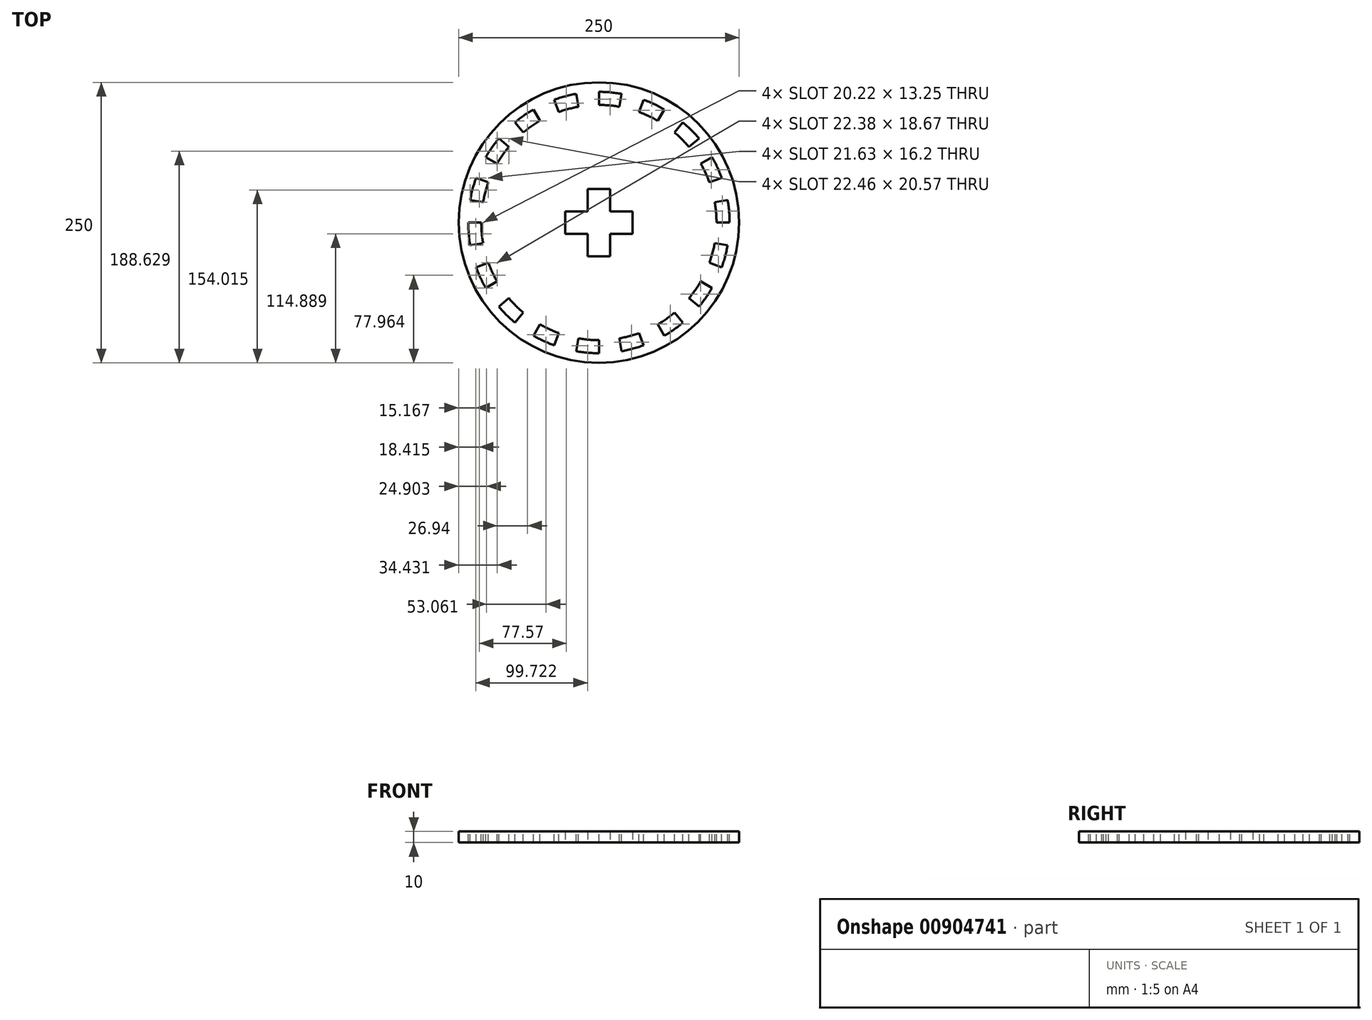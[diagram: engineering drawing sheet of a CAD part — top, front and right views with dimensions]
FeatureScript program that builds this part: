
annotation { "Feature Type Name" : "Feature", "Feature Type Description" : "" }
export const myFeature = defineFeature(function(context is Context, id is Id, definition is map)
    precondition{}
    {
        {
            var Q0;
            Q0=qCreatedBy(makeId("Top.planeOp"),FACE);
            var sketch = newSketch(context, id + "F0", { "sketchPlane" : qUnion([Q0])});
            skCircle(sketch, "E0", {"center": v(0, 0) * mm, "radius": 145 * mm});
            skArc(sketch, "E1", {"start": v(9.54, 136.41) * mm, "mid": v(4.77, 136.66) * mm, "end": v(0, 136.75) * mm});
            skArc(sketch, "E2", {"start": v(8, 114.55) * mm, "mid": v(4, 114.76) * mm, "end": v(0, 114.83) * mm});
            skLineSegment(sketch, "E3", {"start": v(0, 0) * mm, "end": v(0, 38.61) * mm, "construction": true});
            skLineSegment(sketch, "E4", {"start": v(0, 38.61) * mm, "end": v(0, 0) * mm, "construction": true});
            skLineSegment(sketch, "E5", {"start": v(0, 0) * mm, "end": v(-47.77, 0) * mm, "construction": true});
            skLineSegment(sketch, "E6", {"start": v(0, 30) * mm, "end": v(-10, 30) * mm});
            skLineSegment(sketch, "E7", {"start": v(-10, 30) * mm, "end": v(-10, 10) * mm});
            skLineSegment(sketch, "E8", {"start": v(-10, 10) * mm, "end": v(-30, 10) * mm});
            skLineSegment(sketch, "E9", {"start": v(-30, 10) * mm, "end": v(-30, 0) * mm});
            skLineSegment(sketch, "E10.MirrorCS", {"start": v(-30, -10) * mm, "end": v(-30, 0) * mm});
            skLineSegment(sketch, "E11.MirrorCS", {"start": v(-10, -10) * mm, "end": v(-30, -10) * mm});
            skLineSegment(sketch, "E12.MirrorCS", {"start": v(-10, -30) * mm, "end": v(-10, -10) * mm});
            skLineSegment(sketch, "E13.MirrorCS", {"start": v(0, -30) * mm, "end": v(-10, -30) * mm});
            skLineSegment(sketch, "E14.MirrorCS", {"start": v(0, 30) * mm, "end": v(10, 30) * mm});
            skLineSegment(sketch, "E15.MirrorCS", {"start": v(10, 30) * mm, "end": v(10, 10) * mm});
            skLineSegment(sketch, "E16.MirrorCS", {"start": v(10, 10) * mm, "end": v(30, 10) * mm});
            skLineSegment(sketch, "E17.MirrorCS", {"start": v(30, 10) * mm, "end": v(30, 0) * mm});
            skLineSegment(sketch, "E18.MirrorCS", {"start": v(30, -10) * mm, "end": v(30, 0) * mm});
            skLineSegment(sketch, "E19.MirrorCS", {"start": v(10, -10) * mm, "end": v(30, -10) * mm});
            skLineSegment(sketch, "E20.MirrorCS", {"start": v(0, -30) * mm, "end": v(10, -30) * mm});
            skLineSegment(sketch, "E21.MirrorCS", {"start": v(10, -30) * mm, "end": v(10, -10) * mm});
            skLineSegment(sketch, "E22", {"start": v(0, 114.83) * mm, "end": v(0, 136.75) * mm});
            skLineSegment(sketch, "E23", {"start": v(8, 114.55) * mm, "end": v(9.54, 136.41) * mm});
            skArc(sketch, "E24.1.0", {"start": v(-10, 114.4) * mm, "mid": v(-14, 113.98) * mm, "end": v(-17.96, 113.42) * mm});
            skLineSegment(sketch, "E24.1.1", {"start": v(-17.96, 113.42) * mm, "end": v(-21.4, 135.06) * mm});
            skArc(sketch, "E24.1.2", {"start": v(-11.92, 136.23) * mm, "mid": v(-16.67, 135.73) * mm, "end": v(-21.4, 135.06) * mm});
            skLineSegment(sketch, "E24.1.3", {"start": v(-10, 114.4) * mm, "end": v(-11.92, 136.23) * mm});
            skArc(sketch, "E24.2.0", {"start": v(-27.78, 111.42) * mm, "mid": v(-31.65, 110.39) * mm, "end": v(-35.49, 109.21) * mm});
            skLineSegment(sketch, "E24.2.1", {"start": v(-35.49, 109.21) * mm, "end": v(-42.26, 130.05) * mm});
            skArc(sketch, "E24.2.2", {"start": v(-33.08, 132.68) * mm, "mid": v(-37.7, 131.45) * mm, "end": v(-42.26, 130.05) * mm});
            skLineSegment(sketch, "E24.2.3", {"start": v(-27.78, 111.42) * mm, "end": v(-33.08, 132.68) * mm});
            skArc(sketch, "E24.3.0", {"start": v(-44.87, 105.7) * mm, "mid": v(-48.53, 104.07) * mm, "end": v(-52.13, 102.32) * mm});
            skLineSegment(sketch, "E24.3.1", {"start": v(-52.13, 102.32) * mm, "end": v(-62.08, 121.84) * mm});
            skArc(sketch, "E24.3.2", {"start": v(-53.43, 125.88) * mm, "mid": v(-57.8, 123.93) * mm, "end": v(-62.08, 121.84) * mm});
            skLineSegment(sketch, "E24.3.3", {"start": v(-44.87, 105.7) * mm, "end": v(-53.43, 125.88) * mm});
            skArc(sketch, "E24.4.0", {"start": v(-60.85, 97.38) * mm, "mid": v(-64.21, 95.2) * mm, "end": v(-67.5, 92.9) * mm});
            skLineSegment(sketch, "E24.4.1", {"start": v(-67.5, 92.9) * mm, "end": v(-80.38, 110.63) * mm});
            skArc(sketch, "E24.4.2", {"start": v(-72.47, 115.97) * mm, "mid": v(-76.47, 113.37) * mm, "end": v(-80.38, 110.63) * mm});
            skLineSegment(sketch, "E24.4.3", {"start": v(-60.85, 97.38) * mm, "end": v(-72.47, 115.97) * mm});
            skArc(sketch, "E24.5.0", {"start": v(-75.34, 86.67) * mm, "mid": v(-78.32, 83.98) * mm, "end": v(-81.2, 81.2) * mm});
            skLineSegment(sketch, "E24.5.1", {"start": v(-81.2, 81.2) * mm, "end": v(-96.7, 96.7) * mm});
            skArc(sketch, "E24.5.2", {"start": v(-89.71, 103.2) * mm, "mid": v(-93.26, 100.01) * mm, "end": v(-96.7, 96.7) * mm});
            skLineSegment(sketch, "E24.5.3", {"start": v(-75.34, 86.67) * mm, "end": v(-89.71, 103.2) * mm});
            skArc(sketch, "E24.6.0", {"start": v(-87.97, 73.81) * mm, "mid": v(-90.5, 70.7) * mm, "end": v(-92.9, 67.5) * mm});
            skLineSegment(sketch, "E24.6.1", {"start": v(-92.9, 67.5) * mm, "end": v(-110.63, 80.38) * mm});
            skArc(sketch, "E24.6.2", {"start": v(-104.75, 87.9) * mm, "mid": v(-107.76, 84.19) * mm, "end": v(-110.63, 80.38) * mm});
            skLineSegment(sketch, "E24.6.3", {"start": v(-87.97, 73.81) * mm, "end": v(-104.75, 87.9) * mm});
            skArc(sketch, "E24.7.0", {"start": v(-98.43, 59.14) * mm, "mid": v(-100.44, 55.67) * mm, "end": v(-102.32, 52.13) * mm});
            skLineSegment(sketch, "E24.7.1", {"start": v(-102.32, 52.13) * mm, "end": v(-121.84, 62.08) * mm});
            skArc(sketch, "E24.7.2", {"start": v(-117.22, 70.43) * mm, "mid": v(-119.6, 66.3) * mm, "end": v(-121.84, 62.08) * mm});
            skLineSegment(sketch, "E24.7.3", {"start": v(-98.43, 59.14) * mm, "end": v(-117.22, 70.43) * mm});
            skArc(sketch, "E24.8.0", {"start": v(-106.47, 43.02) * mm, "mid": v(-107.9, 39.28) * mm, "end": v(-109.21, 35.49) * mm});
            skLineSegment(sketch, "E24.8.1", {"start": v(-109.21, 35.49) * mm, "end": v(-130.05, 42.26) * mm});
            skArc(sketch, "E24.8.2", {"start": v(-126.79, 51.23) * mm, "mid": v(-128.5, 46.77) * mm, "end": v(-130.05, 42.26) * mm});
            skLineSegment(sketch, "E24.8.3", {"start": v(-106.47, 43.02) * mm, "end": v(-126.79, 51.23) * mm});
            skArc(sketch, "E24.9.0", {"start": v(-111.9, 25.83) * mm, "mid": v(-112.72, 21.91) * mm, "end": v(-113.42, 17.96) * mm});
            skLineSegment(sketch, "E24.9.1", {"start": v(-113.42, 17.96) * mm, "end": v(-135.06, 21.4) * mm});
            skArc(sketch, "E24.9.2", {"start": v(-133.24, 30.76) * mm, "mid": v(-134.23, 26.1) * mm, "end": v(-135.06, 21.4) * mm});
            skLineSegment(sketch, "E24.9.3", {"start": v(-111.9, 25.83) * mm, "end": v(-133.24, 30.76) * mm});
            skArc(sketch, "E24.10.0", {"start": v(-114.55, 8) * mm, "mid": v(-114.76, 4) * mm, "end": v(-114.83, 0) * mm});
            skLineSegment(sketch, "E24.10.1", {"start": v(-114.83, 0) * mm, "end": v(-136.75, 0) * mm});
            skArc(sketch, "E24.10.2", {"start": v(-136.41, 9.54) * mm, "mid": v(-136.66, 4.77) * mm, "end": v(-136.75, 0) * mm});
            skLineSegment(sketch, "E24.10.3", {"start": v(-114.55, 8) * mm, "end": v(-136.41, 9.54) * mm});
            skArc(sketch, "E24.11.0", {"start": v(-114.4, -10) * mm, "mid": v(-113.98, -14) * mm, "end": v(-113.42, -17.96) * mm});
            skLineSegment(sketch, "E24.11.1", {"start": v(-113.42, -17.96) * mm, "end": v(-135.06, -21.4) * mm});
            skArc(sketch, "E24.11.2", {"start": v(-136.23, -11.92) * mm, "mid": v(-135.73, -16.67) * mm, "end": v(-135.06, -21.4) * mm});
            skLineSegment(sketch, "E24.11.3", {"start": v(-114.4, -10) * mm, "end": v(-136.23, -11.92) * mm});
            skArc(sketch, "E24.12.0", {"start": v(-111.42, -27.78) * mm, "mid": v(-110.39, -31.65) * mm, "end": v(-109.21, -35.49) * mm});
            skLineSegment(sketch, "E24.12.1", {"start": v(-109.21, -35.49) * mm, "end": v(-130.05, -42.26) * mm});
            skArc(sketch, "E24.12.2", {"start": v(-132.68, -33.08) * mm, "mid": v(-131.45, -37.7) * mm, "end": v(-130.05, -42.26) * mm});
            skLineSegment(sketch, "E24.12.3", {"start": v(-111.42, -27.78) * mm, "end": v(-132.68, -33.08) * mm});
            skArc(sketch, "E24.13.0", {"start": v(-105.7, -44.87) * mm, "mid": v(-104.07, -48.53) * mm, "end": v(-102.32, -52.13) * mm});
            skLineSegment(sketch, "E24.13.1", {"start": v(-102.32, -52.13) * mm, "end": v(-121.84, -62.08) * mm});
            skArc(sketch, "E24.13.2", {"start": v(-125.88, -53.43) * mm, "mid": v(-123.93, -57.8) * mm, "end": v(-121.84, -62.08) * mm});
            skLineSegment(sketch, "E24.13.3", {"start": v(-105.7, -44.87) * mm, "end": v(-125.88, -53.43) * mm});
            skArc(sketch, "E24.14.0", {"start": v(-97.38, -60.85) * mm, "mid": v(-95.2, -64.21) * mm, "end": v(-92.9, -67.5) * mm});
            skLineSegment(sketch, "E24.14.1", {"start": v(-92.9, -67.5) * mm, "end": v(-110.63, -80.38) * mm});
            skArc(sketch, "E24.14.2", {"start": v(-115.97, -72.47) * mm, "mid": v(-113.37, -76.47) * mm, "end": v(-110.63, -80.38) * mm});
            skLineSegment(sketch, "E24.14.3", {"start": v(-97.38, -60.85) * mm, "end": v(-115.97, -72.47) * mm});
            skArc(sketch, "E24.15.0", {"start": v(-86.67, -75.34) * mm, "mid": v(-83.98, -78.32) * mm, "end": v(-81.2, -81.2) * mm});
            skLineSegment(sketch, "E24.15.1", {"start": v(-81.2, -81.2) * mm, "end": v(-96.7, -96.7) * mm});
            skArc(sketch, "E24.15.2", {"start": v(-103.2, -89.71) * mm, "mid": v(-100.01, -93.26) * mm, "end": v(-96.7, -96.7) * mm});
            skLineSegment(sketch, "E24.15.3", {"start": v(-86.67, -75.34) * mm, "end": v(-103.2, -89.71) * mm});
            skArc(sketch, "E24.16.0", {"start": v(-73.81, -87.97) * mm, "mid": v(-70.7, -90.5) * mm, "end": v(-67.5, -92.9) * mm});
            skLineSegment(sketch, "E24.16.1", {"start": v(-67.5, -92.9) * mm, "end": v(-80.38, -110.63) * mm});
            skArc(sketch, "E24.16.2", {"start": v(-87.9, -104.75) * mm, "mid": v(-84.19, -107.76) * mm, "end": v(-80.38, -110.63) * mm});
            skLineSegment(sketch, "E24.16.3", {"start": v(-73.81, -87.97) * mm, "end": v(-87.9, -104.75) * mm});
            skArc(sketch, "E24.17.0", {"start": v(-59.14, -98.43) * mm, "mid": v(-55.67, -100.44) * mm, "end": v(-52.13, -102.32) * mm});
            skLineSegment(sketch, "E24.17.1", {"start": v(-52.13, -102.32) * mm, "end": v(-62.08, -121.84) * mm});
            skArc(sketch, "E24.17.2", {"start": v(-70.43, -117.22) * mm, "mid": v(-66.3, -119.6) * mm, "end": v(-62.08, -121.84) * mm});
            skLineSegment(sketch, "E24.17.3", {"start": v(-59.14, -98.43) * mm, "end": v(-70.43, -117.22) * mm});
            skArc(sketch, "E24.18.0", {"start": v(-43.02, -106.47) * mm, "mid": v(-39.28, -107.9) * mm, "end": v(-35.49, -109.21) * mm});
            skLineSegment(sketch, "E24.18.1", {"start": v(-35.49, -109.21) * mm, "end": v(-42.26, -130.05) * mm});
            skArc(sketch, "E24.18.2", {"start": v(-51.23, -126.79) * mm, "mid": v(-46.77, -128.5) * mm, "end": v(-42.26, -130.05) * mm});
            skLineSegment(sketch, "E24.18.3", {"start": v(-43.02, -106.47) * mm, "end": v(-51.23, -126.79) * mm});
            skArc(sketch, "E24.19.0", {"start": v(-25.83, -111.9) * mm, "mid": v(-21.91, -112.72) * mm, "end": v(-17.96, -113.42) * mm});
            skLineSegment(sketch, "E24.19.1", {"start": v(-17.96, -113.42) * mm, "end": v(-21.4, -135.06) * mm});
            skArc(sketch, "E24.19.2", {"start": v(-30.76, -133.24) * mm, "mid": v(-26.1, -134.23) * mm, "end": v(-21.4, -135.06) * mm});
            skLineSegment(sketch, "E24.19.3", {"start": v(-25.83, -111.9) * mm, "end": v(-30.76, -133.24) * mm});
            skArc(sketch, "E24.20.0", {"start": v(-8, -114.55) * mm, "mid": v(-4, -114.76) * mm, "end": v(0, -114.83) * mm});
            skLineSegment(sketch, "E24.20.1", {"start": v(0, -114.83) * mm, "end": v(0, -136.75) * mm});
            skArc(sketch, "E24.20.2", {"start": v(-9.54, -136.41) * mm, "mid": v(-4.77, -136.66) * mm, "end": v(0, -136.75) * mm});
            skLineSegment(sketch, "E24.20.3", {"start": v(-8, -114.55) * mm, "end": v(-9.54, -136.41) * mm});
            skArc(sketch, "E24.21.0", {"start": v(10, -114.4) * mm, "mid": v(14, -113.98) * mm, "end": v(17.96, -113.42) * mm});
            skLineSegment(sketch, "E24.21.1", {"start": v(17.96, -113.42) * mm, "end": v(21.4, -135.06) * mm});
            skArc(sketch, "E24.21.2", {"start": v(11.92, -136.23) * mm, "mid": v(16.67, -135.73) * mm, "end": v(21.4, -135.06) * mm});
            skLineSegment(sketch, "E24.21.3", {"start": v(10, -114.4) * mm, "end": v(11.92, -136.23) * mm});
            skArc(sketch, "E24.22.0", {"start": v(27.78, -111.42) * mm, "mid": v(31.65, -110.39) * mm, "end": v(35.49, -109.21) * mm});
            skLineSegment(sketch, "E24.22.1", {"start": v(35.49, -109.21) * mm, "end": v(42.26, -130.05) * mm});
            skArc(sketch, "E24.22.2", {"start": v(33.08, -132.68) * mm, "mid": v(37.7, -131.45) * mm, "end": v(42.26, -130.05) * mm});
            skLineSegment(sketch, "E24.22.3", {"start": v(27.78, -111.42) * mm, "end": v(33.08, -132.68) * mm});
            skArc(sketch, "E24.23.0", {"start": v(44.87, -105.7) * mm, "mid": v(48.53, -104.07) * mm, "end": v(52.13, -102.32) * mm});
            skLineSegment(sketch, "E24.23.1", {"start": v(52.13, -102.32) * mm, "end": v(62.08, -121.84) * mm});
            skArc(sketch, "E24.23.2", {"start": v(53.43, -125.88) * mm, "mid": v(57.8, -123.93) * mm, "end": v(62.08, -121.84) * mm});
            skLineSegment(sketch, "E24.23.3", {"start": v(44.87, -105.7) * mm, "end": v(53.43, -125.88) * mm});
            skArc(sketch, "E24.24.0", {"start": v(60.85, -97.38) * mm, "mid": v(64.21, -95.2) * mm, "end": v(67.5, -92.9) * mm});
            skLineSegment(sketch, "E24.24.1", {"start": v(67.5, -92.9) * mm, "end": v(80.38, -110.63) * mm});
            skArc(sketch, "E24.24.2", {"start": v(72.47, -115.97) * mm, "mid": v(76.47, -113.37) * mm, "end": v(80.38, -110.63) * mm});
            skLineSegment(sketch, "E24.24.3", {"start": v(60.85, -97.38) * mm, "end": v(72.47, -115.97) * mm});
            skArc(sketch, "E24.25.0", {"start": v(75.34, -86.67) * mm, "mid": v(78.32, -83.98) * mm, "end": v(81.2, -81.2) * mm});
            skLineSegment(sketch, "E24.25.1", {"start": v(81.2, -81.2) * mm, "end": v(96.7, -96.7) * mm});
            skArc(sketch, "E24.25.2", {"start": v(89.71, -103.2) * mm, "mid": v(93.26, -100.01) * mm, "end": v(96.7, -96.7) * mm});
            skLineSegment(sketch, "E24.25.3", {"start": v(75.34, -86.67) * mm, "end": v(89.71, -103.2) * mm});
            skArc(sketch, "E24.26.0", {"start": v(87.97, -73.81) * mm, "mid": v(90.5, -70.7) * mm, "end": v(92.9, -67.5) * mm});
            skLineSegment(sketch, "E24.26.1", {"start": v(92.9, -67.5) * mm, "end": v(110.63, -80.38) * mm});
            skArc(sketch, "E24.26.2", {"start": v(104.75, -87.9) * mm, "mid": v(107.76, -84.19) * mm, "end": v(110.63, -80.38) * mm});
            skLineSegment(sketch, "E24.26.3", {"start": v(87.97, -73.81) * mm, "end": v(104.75, -87.9) * mm});
            skArc(sketch, "E24.27.0", {"start": v(98.43, -59.14) * mm, "mid": v(100.44, -55.67) * mm, "end": v(102.32, -52.13) * mm});
            skLineSegment(sketch, "E24.27.1", {"start": v(102.32, -52.13) * mm, "end": v(121.84, -62.08) * mm});
            skArc(sketch, "E24.27.2", {"start": v(117.22, -70.43) * mm, "mid": v(119.6, -66.3) * mm, "end": v(121.84, -62.08) * mm});
            skLineSegment(sketch, "E24.27.3", {"start": v(98.43, -59.14) * mm, "end": v(117.22, -70.43) * mm});
            skArc(sketch, "E24.28.0", {"start": v(106.47, -43.02) * mm, "mid": v(107.9, -39.28) * mm, "end": v(109.21, -35.49) * mm});
            skLineSegment(sketch, "E24.28.1", {"start": v(109.21, -35.49) * mm, "end": v(130.05, -42.26) * mm});
            skArc(sketch, "E24.28.2", {"start": v(126.79, -51.23) * mm, "mid": v(128.5, -46.77) * mm, "end": v(130.05, -42.26) * mm});
            skLineSegment(sketch, "E24.28.3", {"start": v(106.47, -43.02) * mm, "end": v(126.79, -51.23) * mm});
            skArc(sketch, "E24.29.0", {"start": v(111.9, -25.83) * mm, "mid": v(112.72, -21.91) * mm, "end": v(113.42, -17.96) * mm});
            skLineSegment(sketch, "E24.29.1", {"start": v(113.42, -17.96) * mm, "end": v(135.06, -21.4) * mm});
            skArc(sketch, "E24.29.2", {"start": v(133.24, -30.76) * mm, "mid": v(134.23, -26.1) * mm, "end": v(135.06, -21.4) * mm});
            skLineSegment(sketch, "E24.29.3", {"start": v(111.9, -25.83) * mm, "end": v(133.24, -30.76) * mm});
            skArc(sketch, "E24.30.0", {"start": v(114.55, -8) * mm, "mid": v(114.76, -4) * mm, "end": v(114.83, 0) * mm});
            skLineSegment(sketch, "E24.30.1", {"start": v(114.83, 0) * mm, "end": v(136.75, 0) * mm});
            skArc(sketch, "E24.30.2", {"start": v(136.41, -9.54) * mm, "mid": v(136.66, -4.77) * mm, "end": v(136.75, 0) * mm});
            skLineSegment(sketch, "E24.30.3", {"start": v(114.55, -8) * mm, "end": v(136.41, -9.54) * mm});
            skArc(sketch, "E24.31.0", {"start": v(114.4, 10) * mm, "mid": v(113.98, 14) * mm, "end": v(113.42, 17.96) * mm});
            skLineSegment(sketch, "E24.31.1", {"start": v(113.42, 17.96) * mm, "end": v(135.06, 21.4) * mm});
            skArc(sketch, "E24.31.2", {"start": v(136.23, 11.92) * mm, "mid": v(135.73, 16.67) * mm, "end": v(135.06, 21.4) * mm});
            skLineSegment(sketch, "E24.31.3", {"start": v(114.4, 10) * mm, "end": v(136.23, 11.92) * mm});
            skArc(sketch, "E24.32.0", {"start": v(111.42, 27.78) * mm, "mid": v(110.39, 31.65) * mm, "end": v(109.21, 35.49) * mm});
            skLineSegment(sketch, "E24.32.1", {"start": v(109.21, 35.49) * mm, "end": v(130.05, 42.26) * mm});
            skArc(sketch, "E24.32.2", {"start": v(132.68, 33.08) * mm, "mid": v(131.45, 37.7) * mm, "end": v(130.05, 42.26) * mm});
            skLineSegment(sketch, "E24.32.3", {"start": v(111.42, 27.78) * mm, "end": v(132.68, 33.08) * mm});
            skArc(sketch, "E24.33.0", {"start": v(105.7, 44.87) * mm, "mid": v(104.07, 48.53) * mm, "end": v(102.32, 52.13) * mm});
            skLineSegment(sketch, "E24.33.1", {"start": v(102.32, 52.13) * mm, "end": v(121.84, 62.08) * mm});
            skArc(sketch, "E24.33.2", {"start": v(125.88, 53.43) * mm, "mid": v(123.93, 57.8) * mm, "end": v(121.84, 62.08) * mm});
            skLineSegment(sketch, "E24.33.3", {"start": v(105.7, 44.87) * mm, "end": v(125.88, 53.43) * mm});
            skArc(sketch, "E24.34.0", {"start": v(97.38, 60.85) * mm, "mid": v(95.2, 64.21) * mm, "end": v(92.9, 67.5) * mm});
            skLineSegment(sketch, "E24.34.1", {"start": v(92.9, 67.5) * mm, "end": v(110.63, 80.38) * mm});
            skArc(sketch, "E24.34.2", {"start": v(115.97, 72.47) * mm, "mid": v(113.37, 76.47) * mm, "end": v(110.63, 80.38) * mm});
            skLineSegment(sketch, "E24.34.3", {"start": v(97.38, 60.85) * mm, "end": v(115.97, 72.47) * mm});
            skArc(sketch, "E24.35.0", {"start": v(86.67, 75.34) * mm, "mid": v(83.98, 78.32) * mm, "end": v(81.2, 81.2) * mm});
            skLineSegment(sketch, "E24.35.1", {"start": v(81.2, 81.2) * mm, "end": v(96.7, 96.7) * mm});
            skArc(sketch, "E24.35.2", {"start": v(103.2, 89.71) * mm, "mid": v(100.01, 93.26) * mm, "end": v(96.7, 96.7) * mm});
            skLineSegment(sketch, "E24.35.3", {"start": v(86.67, 75.34) * mm, "end": v(103.2, 89.71) * mm});
            skArc(sketch, "E24.36.0", {"start": v(73.81, 87.97) * mm, "mid": v(70.7, 90.5) * mm, "end": v(67.5, 92.9) * mm});
            skLineSegment(sketch, "E24.36.1", {"start": v(67.5, 92.9) * mm, "end": v(80.38, 110.63) * mm});
            skArc(sketch, "E24.36.2", {"start": v(87.9, 104.75) * mm, "mid": v(84.19, 107.76) * mm, "end": v(80.38, 110.63) * mm});
            skLineSegment(sketch, "E24.36.3", {"start": v(73.81, 87.97) * mm, "end": v(87.9, 104.75) * mm});
            skArc(sketch, "E24.37.0", {"start": v(59.14, 98.43) * mm, "mid": v(55.67, 100.44) * mm, "end": v(52.13, 102.32) * mm});
            skLineSegment(sketch, "E24.37.1", {"start": v(52.13, 102.32) * mm, "end": v(62.08, 121.84) * mm});
            skArc(sketch, "E24.37.2", {"start": v(70.43, 117.22) * mm, "mid": v(66.3, 119.6) * mm, "end": v(62.08, 121.84) * mm});
            skLineSegment(sketch, "E24.37.3", {"start": v(59.14, 98.43) * mm, "end": v(70.43, 117.22) * mm});
            skArc(sketch, "E24.38.0", {"start": v(43.02, 106.47) * mm, "mid": v(39.28, 107.9) * mm, "end": v(35.49, 109.21) * mm});
            skLineSegment(sketch, "E24.38.1", {"start": v(35.49, 109.21) * mm, "end": v(42.26, 130.05) * mm});
            skArc(sketch, "E24.38.2", {"start": v(51.23, 126.79) * mm, "mid": v(46.77, 128.5) * mm, "end": v(42.26, 130.05) * mm});
            skLineSegment(sketch, "E24.38.3", {"start": v(43.02, 106.47) * mm, "end": v(51.23, 126.79) * mm});
            skArc(sketch, "E24.39.0", {"start": v(25.83, 111.9) * mm, "mid": v(21.91, 112.72) * mm, "end": v(17.96, 113.42) * mm});
            skLineSegment(sketch, "E24.39.1", {"start": v(17.96, 113.42) * mm, "end": v(21.4, 135.06) * mm});
            skArc(sketch, "E24.39.2", {"start": v(30.76, 133.24) * mm, "mid": v(26.1, 134.23) * mm, "end": v(21.4, 135.06) * mm});
            skLineSegment(sketch, "E24.39.3", {"start": v(25.83, 111.9) * mm, "end": v(30.76, 133.24) * mm});
            skCircle(sketch, "E25", {"center": v(0, 0) * mm, "radius": 50 * mm});
            skSolve(sketch);
        }
        {
            var Q0;
            Q0=makeQuery(id+"F0.imprint","IMPRINT",FACE,{"disambiguationData":[TD([[makeQuery(id+"F0.imprint","IMPRINT",EDGE,{"derivedFrom":sQuery(id+"F0.wireOp",EDGE,"E6")}),-1.0]])]});
            extrude(context, id + "F1", {"entities" : qUnion([Q0]), "depth" : 10 * mm, "offsetDistance" : 25 * mm});
        }
        {
            var Q0;
            Q0=makeQuery(id+"F1.opExtrude","CAP_FACE",FACE,{"disambiguationData":[OSD([sQuery(id+"F0.wireOp",EDGE,"E6"),sQuery(id+"F0.wireOp",EDGE,"E7"),sQuery(id+"F0.wireOp",EDGE,"E8"),sQuery(id+"F0.wireOp",EDGE,"E9"),sQuery(id+"F0.wireOp",EDGE,"E10.MirrorCS"),sQuery(id+"F0.wireOp",EDGE,"E11.MirrorCS"),sQuery(id+"F0.wireOp",EDGE,"E12.MirrorCS"),sQuery(id+"F0.wireOp",EDGE,"E13.MirrorCS"),sQuery(id+"F0.wireOp",EDGE,"E14.MirrorCS"),sQuery(id+"F0.wireOp",EDGE,"E15.MirrorCS"),sQuery(id+"F0.wireOp",EDGE,"E16.MirrorCS"),sQuery(id+"F0.wireOp",EDGE,"E17.MirrorCS"),sQuery(id+"F0.wireOp",EDGE,"E18.MirrorCS"),sQuery(id+"F0.wireOp",EDGE,"E19.MirrorCS"),sQuery(id+"F0.wireOp",EDGE,"E20.MirrorCS"),sQuery(id+"F0.wireOp",EDGE,"E21.MirrorCS"),sQuery(id+"F0.wireOp",EDGE,"E25")])],"isStart":false});
            var sketch = newSketch(context, id + "F2", { "sketchPlane" : qUnion([Q0])});
            skCircle(sketch, "E26", {"center": v(0, 0) * mm, "radius": 125 * mm});
            skCircle(sketch, "E27", {"center": v(0, 0) * mm, "radius": 40.45 * mm});
            skSolve(sketch);
        }
        {
            var Q0;
            Q0=qSketchRegion(id+"F2",true);
            extrude(context, id + "F3", {"entities" : qUnion([Q0]), "operationType" : NewBodyOperationType.ADD, "oppositeDirection" : true, "depth" : 10 * mm, "offsetDistance" : 25 * mm});
        }
        {
            var Q0;
            Q0=makeQuery(id+"F3.boolean.opBoolean","MERGE",FACE,{"derivedFrom":[makeQuery(id+"F1.opExtrude","CAP_FACE",FACE,{"disambiguationData":[OSD([sQuery(id+"F0.wireOp",EDGE,"E6"),sQuery(id+"F0.wireOp",EDGE,"E7"),sQuery(id+"F0.wireOp",EDGE,"E8"),sQuery(id+"F0.wireOp",EDGE,"E9"),sQuery(id+"F0.wireOp",EDGE,"E10.MirrorCS"),sQuery(id+"F0.wireOp",EDGE,"E11.MirrorCS"),sQuery(id+"F0.wireOp",EDGE,"E12.MirrorCS"),sQuery(id+"F0.wireOp",EDGE,"E13.MirrorCS"),sQuery(id+"F0.wireOp",EDGE,"E14.MirrorCS"),sQuery(id+"F0.wireOp",EDGE,"E15.MirrorCS"),sQuery(id+"F0.wireOp",EDGE,"E16.MirrorCS"),sQuery(id+"F0.wireOp",EDGE,"E17.MirrorCS"),sQuery(id+"F0.wireOp",EDGE,"E18.MirrorCS"),sQuery(id+"F0.wireOp",EDGE,"E19.MirrorCS"),sQuery(id+"F0.wireOp",EDGE,"E20.MirrorCS"),sQuery(id+"F0.wireOp",EDGE,"E21.MirrorCS"),sQuery(id+"F0.wireOp",EDGE,"E25")])],"isStart":false}),makeQuery(id+"F3.opExtrude","CAP_FACE",FACE,{"disambiguationData":[OSD([sQuery(id+"F2.wireOp",EDGE,"E26"),sQuery(id+"F2.wireOp",EDGE,"E27")])],"isStart":true})]});
            var sketch = newSketch(context, id + "F4", { "sketchPlane" : qUnion([Q0])});
            skLineSegment(sketch, "E28", {"start": v(0, 104.8) * mm, "end": v(0, 116.46) * mm});
            skLineSegment(sketch, "E29", {"start": v(0, 116.46) * mm, "end": v(0, 104.8) * mm});
            skLineSegment(sketch, "E30", {"start": v(18.2, 103.21) * mm, "end": v(20.22, 114.69) * mm});
            skArc(sketch, "E31", {"start": v(20.22, 114.69) * mm, "mid": v(10.15, 116.01) * mm, "end": v(0, 116.46) * mm});
            skArc(sketch, "E32", {"start": v(18.2, 103.21) * mm, "mid": v(9.13, 104.4) * mm, "end": v(0, 104.8) * mm});
            skArc(sketch, "E33.1.0", {"start": v(-18.2, 103.21) * mm, "mid": v(-27.12, 101.23) * mm, "end": v(-35.84, 98.48) * mm});
            skLineSegment(sketch, "E33.1.1", {"start": v(-39.83, 109.43) * mm, "end": v(-35.84, 98.48) * mm});
            skArc(sketch, "E33.1.2", {"start": v(-20.22, 114.69) * mm, "mid": v(-30.14, 112.49) * mm, "end": v(-39.83, 109.43) * mm});
            skLineSegment(sketch, "E33.1.3", {"start": v(-18.2, 103.21) * mm, "end": v(-20.22, 114.69) * mm});
            skArc(sketch, "E33.2.0", {"start": v(-52.4, 90.76) * mm, "mid": v(-60.11, 85.85) * mm, "end": v(-67.37, 80.28) * mm});
            skLineSegment(sketch, "E33.2.1", {"start": v(-74.86, 89.21) * mm, "end": v(-67.37, 80.28) * mm});
            skArc(sketch, "E33.2.2", {"start": v(-58.23, 100.85) * mm, "mid": v(-66.8, 95.4) * mm, "end": v(-74.86, 89.21) * mm});
            skLineSegment(sketch, "E33.2.3", {"start": v(-52.4, 90.76) * mm, "end": v(-58.23, 100.85) * mm});
            skArc(sketch, "E33.3.0", {"start": v(-80.28, 67.37) * mm, "mid": v(-85.85, 60.11) * mm, "end": v(-90.76, 52.4) * mm});
            skLineSegment(sketch, "E33.3.1", {"start": v(-100.85, 58.23) * mm, "end": v(-90.76, 52.4) * mm});
            skArc(sketch, "E33.3.2", {"start": v(-89.21, 74.86) * mm, "mid": v(-95.4, 66.8) * mm, "end": v(-100.85, 58.23) * mm});
            skLineSegment(sketch, "E33.3.3", {"start": v(-80.28, 67.37) * mm, "end": v(-89.21, 74.86) * mm});
            skArc(sketch, "E33.4.0", {"start": v(-98.48, 35.84) * mm, "mid": v(-101.23, 27.12) * mm, "end": v(-103.21, 18.2) * mm});
            skLineSegment(sketch, "E33.4.1", {"start": v(-114.69, 20.22) * mm, "end": v(-103.21, 18.2) * mm});
            skArc(sketch, "E33.4.2", {"start": v(-109.43, 39.83) * mm, "mid": v(-112.49, 30.14) * mm, "end": v(-114.69, 20.22) * mm});
            skLineSegment(sketch, "E33.4.3", {"start": v(-98.48, 35.84) * mm, "end": v(-109.43, 39.83) * mm});
            skArc(sketch, "E33.5.0", {"start": v(-104.8, 0) * mm, "mid": v(-104.4, -9.13) * mm, "end": v(-103.21, -18.2) * mm});
            skLineSegment(sketch, "E33.5.1", {"start": v(-114.69, -20.22) * mm, "end": v(-103.21, -18.2) * mm});
            skArc(sketch, "E33.5.2", {"start": v(-116.46, 0) * mm, "mid": v(-116.01, -10.15) * mm, "end": v(-114.69, -20.22) * mm});
            skLineSegment(sketch, "E33.5.3", {"start": v(-104.8, 0) * mm, "end": v(-116.46, 0) * mm});
            skArc(sketch, "E33.6.0", {"start": v(-98.48, -35.84) * mm, "mid": v(-94.98, -44.3) * mm, "end": v(-90.76, -52.4) * mm});
            skLineSegment(sketch, "E33.6.1", {"start": v(-100.85, -58.23) * mm, "end": v(-90.76, -52.4) * mm});
            skArc(sketch, "E33.6.2", {"start": v(-109.43, -39.83) * mm, "mid": v(-105.55, -49.22) * mm, "end": v(-100.85, -58.23) * mm});
            skLineSegment(sketch, "E33.6.3", {"start": v(-98.48, -35.84) * mm, "end": v(-109.43, -39.83) * mm});
            skArc(sketch, "E33.7.0", {"start": v(-80.28, -67.37) * mm, "mid": v(-74.1, -74.1) * mm, "end": v(-67.37, -80.28) * mm});
            skLineSegment(sketch, "E33.7.1", {"start": v(-74.86, -89.21) * mm, "end": v(-67.37, -80.28) * mm});
            skArc(sketch, "E33.7.2", {"start": v(-89.21, -74.86) * mm, "mid": v(-82.35, -82.35) * mm, "end": v(-74.86, -89.21) * mm});
            skLineSegment(sketch, "E33.7.3", {"start": v(-80.28, -67.37) * mm, "end": v(-89.21, -74.86) * mm});
            skArc(sketch, "E33.8.0", {"start": v(-52.4, -90.76) * mm, "mid": v(-44.3, -94.98) * mm, "end": v(-35.84, -98.48) * mm});
            skLineSegment(sketch, "E33.8.1", {"start": v(-39.83, -109.43) * mm, "end": v(-35.84, -98.48) * mm});
            skArc(sketch, "E33.8.2", {"start": v(-58.23, -100.85) * mm, "mid": v(-49.22, -105.55) * mm, "end": v(-39.83, -109.43) * mm});
            skLineSegment(sketch, "E33.8.3", {"start": v(-52.4, -90.76) * mm, "end": v(-58.23, -100.85) * mm});
            skArc(sketch, "E33.9.0", {"start": v(-18.2, -103.21) * mm, "mid": v(-9.13, -104.4) * mm, "end": v(0, -104.8) * mm});
            skLineSegment(sketch, "E33.9.1", {"start": v(0, -116.46) * mm, "end": v(0, -104.8) * mm});
            skArc(sketch, "E33.9.2", {"start": v(-20.22, -114.69) * mm, "mid": v(-10.15, -116.01) * mm, "end": v(0, -116.46) * mm});
            skLineSegment(sketch, "E33.9.3", {"start": v(-18.2, -103.21) * mm, "end": v(-20.22, -114.69) * mm});
            skArc(sketch, "E33.10.0", {"start": v(18.2, -103.21) * mm, "mid": v(27.12, -101.23) * mm, "end": v(35.84, -98.48) * mm});
            skLineSegment(sketch, "E33.10.1", {"start": v(39.83, -109.43) * mm, "end": v(35.84, -98.48) * mm});
            skArc(sketch, "E33.10.2", {"start": v(20.22, -114.69) * mm, "mid": v(30.14, -112.49) * mm, "end": v(39.83, -109.43) * mm});
            skLineSegment(sketch, "E33.10.3", {"start": v(18.2, -103.21) * mm, "end": v(20.22, -114.69) * mm});
            skArc(sketch, "E33.11.0", {"start": v(52.4, -90.76) * mm, "mid": v(60.11, -85.85) * mm, "end": v(67.37, -80.28) * mm});
            skLineSegment(sketch, "E33.11.1", {"start": v(74.86, -89.21) * mm, "end": v(67.37, -80.28) * mm});
            skArc(sketch, "E33.11.2", {"start": v(58.23, -100.85) * mm, "mid": v(66.8, -95.4) * mm, "end": v(74.86, -89.21) * mm});
            skLineSegment(sketch, "E33.11.3", {"start": v(52.4, -90.76) * mm, "end": v(58.23, -100.85) * mm});
            skArc(sketch, "E33.12.0", {"start": v(80.28, -67.37) * mm, "mid": v(85.85, -60.11) * mm, "end": v(90.76, -52.4) * mm});
            skLineSegment(sketch, "E33.12.1", {"start": v(100.85, -58.23) * mm, "end": v(90.76, -52.4) * mm});
            skArc(sketch, "E33.12.2", {"start": v(89.21, -74.86) * mm, "mid": v(95.4, -66.8) * mm, "end": v(100.85, -58.23) * mm});
            skLineSegment(sketch, "E33.12.3", {"start": v(80.28, -67.37) * mm, "end": v(89.21, -74.86) * mm});
            skArc(sketch, "E33.13.0", {"start": v(98.48, -35.84) * mm, "mid": v(101.23, -27.12) * mm, "end": v(103.21, -18.2) * mm});
            skLineSegment(sketch, "E33.13.1", {"start": v(114.69, -20.22) * mm, "end": v(103.21, -18.2) * mm});
            skArc(sketch, "E33.13.2", {"start": v(109.43, -39.83) * mm, "mid": v(112.49, -30.14) * mm, "end": v(114.69, -20.22) * mm});
            skLineSegment(sketch, "E33.13.3", {"start": v(98.48, -35.84) * mm, "end": v(109.43, -39.83) * mm});
            skArc(sketch, "E33.14.0", {"start": v(104.8, 0) * mm, "mid": v(104.4, 9.13) * mm, "end": v(103.21, 18.2) * mm});
            skLineSegment(sketch, "E33.14.1", {"start": v(114.69, 20.22) * mm, "end": v(103.21, 18.2) * mm});
            skArc(sketch, "E33.14.2", {"start": v(116.46, 0) * mm, "mid": v(116.01, 10.15) * mm, "end": v(114.69, 20.22) * mm});
            skLineSegment(sketch, "E33.14.3", {"start": v(104.8, 0) * mm, "end": v(116.46, 0) * mm});
            skArc(sketch, "E33.15.0", {"start": v(98.48, 35.84) * mm, "mid": v(94.98, 44.3) * mm, "end": v(90.76, 52.4) * mm});
            skLineSegment(sketch, "E33.15.1", {"start": v(100.85, 58.23) * mm, "end": v(90.76, 52.4) * mm});
            skArc(sketch, "E33.15.2", {"start": v(109.43, 39.83) * mm, "mid": v(105.55, 49.22) * mm, "end": v(100.85, 58.23) * mm});
            skLineSegment(sketch, "E33.15.3", {"start": v(98.48, 35.84) * mm, "end": v(109.43, 39.83) * mm});
            skArc(sketch, "E33.16.0", {"start": v(80.28, 67.37) * mm, "mid": v(74.1, 74.1) * mm, "end": v(67.37, 80.28) * mm});
            skLineSegment(sketch, "E33.16.1", {"start": v(74.86, 89.21) * mm, "end": v(67.37, 80.28) * mm});
            skArc(sketch, "E33.16.2", {"start": v(89.21, 74.86) * mm, "mid": v(82.35, 82.35) * mm, "end": v(74.86, 89.21) * mm});
            skLineSegment(sketch, "E33.16.3", {"start": v(80.28, 67.37) * mm, "end": v(89.21, 74.86) * mm});
            skArc(sketch, "E33.17.0", {"start": v(52.4, 90.76) * mm, "mid": v(44.3, 94.98) * mm, "end": v(35.84, 98.48) * mm});
            skLineSegment(sketch, "E33.17.1", {"start": v(39.83, 109.43) * mm, "end": v(35.84, 98.48) * mm});
            skArc(sketch, "E33.17.2", {"start": v(58.23, 100.85) * mm, "mid": v(49.22, 105.55) * mm, "end": v(39.83, 109.43) * mm});
            skLineSegment(sketch, "E33.17.3", {"start": v(52.4, 90.76) * mm, "end": v(58.23, 100.85) * mm});
            skSolve(sketch);
        }
        {
            var Q0;
            Q0=qSketchRegion(id+"F4",true);
            extrude(context, id + "F5", {"entities" : qUnion([Q0]), "operationType" : NewBodyOperationType.REMOVE, "oppositeDirection" : true, "depth" : 25 * mm, "offsetDistance" : 25 * mm});
        }
    });
